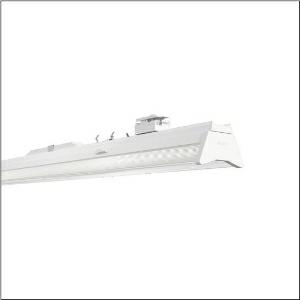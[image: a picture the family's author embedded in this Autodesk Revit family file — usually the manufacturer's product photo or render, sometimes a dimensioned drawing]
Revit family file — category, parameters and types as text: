
# Revit family: licross_r__21_performance_mo_52tm16dn46xg_f566
name_source: partatom
category: Lighting Fixtures
units: mm (PartAtom-declared; Revit-internal decimal feet)

## family parameters
Cut with Voids When Loaded = No
Host = Face
Light Source = No
Part Type = Normal
Room Calculation Point = No
Round Connector Dimension = Use Diameter
Shared = No

## types (1)
- --- (1 x LED, 6000 lm, 32.7 W, 4000K)
    Apparent Load = 33 VA
    CIE Flux Codes = 66 88 96 79 100
    Color Rendering = 80
    Color Temperature = 4000K
    Default Elevation = 1800 mm
    Description = Licross® 21 Performance MO, luminaire insert, of sheet steel, galvanised, coil coated, white, length: 1.500mm, width: 120mm, height: 123mm, LED rated luminous flux: 6.000lm, light colour: 840, control gear: DALI 2, with plug, 5-pole, with phase selection, mains connection: 220..240V, AC, 50/60Hz, rated input power: 33W, halogen-free wiring, primary light control with lens, of plastic, primary optical cover: cover, of PMMA, light emission: direct/indirect distribution, primary light characteristic: symmetric, protection rating (complete): IP40, insulation class (complete): insulation class I (protective earthing), certification: CE, ENEC, UKCA, protection symbol: D if used in an environment without relevant dust loads with corresponding accessories, impact resistance: IK06, permissible ambient temperature for indoor applications: -25..+45°C, corresponds to IFS (International Featured Standards) requirements for safety and quality in the food industry, reducing of maximum allowable ambient temperature of 5°C with ceiling mounting, LABS conformity tested according to VDMA 24364:2018-05, packaging unit: 1 piece
    Height = 114 mm
    Lamp = 1 x LED
    Lamp Light Flux = 6000 lm
    Lamp Power = 32.7 W
    Lamp count = 1
    Length = 1500 mm
    Luminous efficacy = 183 lm/W
    Manufacturer = Siteco
    ModVariant = No
    Model = 52TM16DN46XG
    Mounting Place = Ceiling
    Mounting Type = Pendant
    Number of Poles = 1
    OnlyDefault = Yes
    Power Factor = 1
    Product Name = Licross® 21 Performance MO
    Product group = luminaire insert
    ProductGroupID = 902
    Protection Class = Protection class I
    Protection Degree = IP 40
    RLX_Detail_Level = 1
    RLX_Emergency_Light_Flux = 0 lm
    RLX_Emergency_Type = 0
    RLX_Emergency_Type_DB = No
    RlxData = <blob elided: 33665 chars, md5=6fec304d>
    Socket = socket
    Standby Power = 0 W
    System Light Flux = 6000 lm
    System Power = 33 W
    Type Comments = factory setting: luminous flux: 100 % | dim-lin: 254 | 222 mA
    Type Image = l_1256138.jpg
    URL = http://relux.com
    VarID = @adj_129268
    Voltage = 0 V
    Weight = 0.00 kg
    Width = 120 mm

## geometry (parser evidence)
native form markers: Blend x4, Sweep x12
no freeform markers — native parametric forms only
